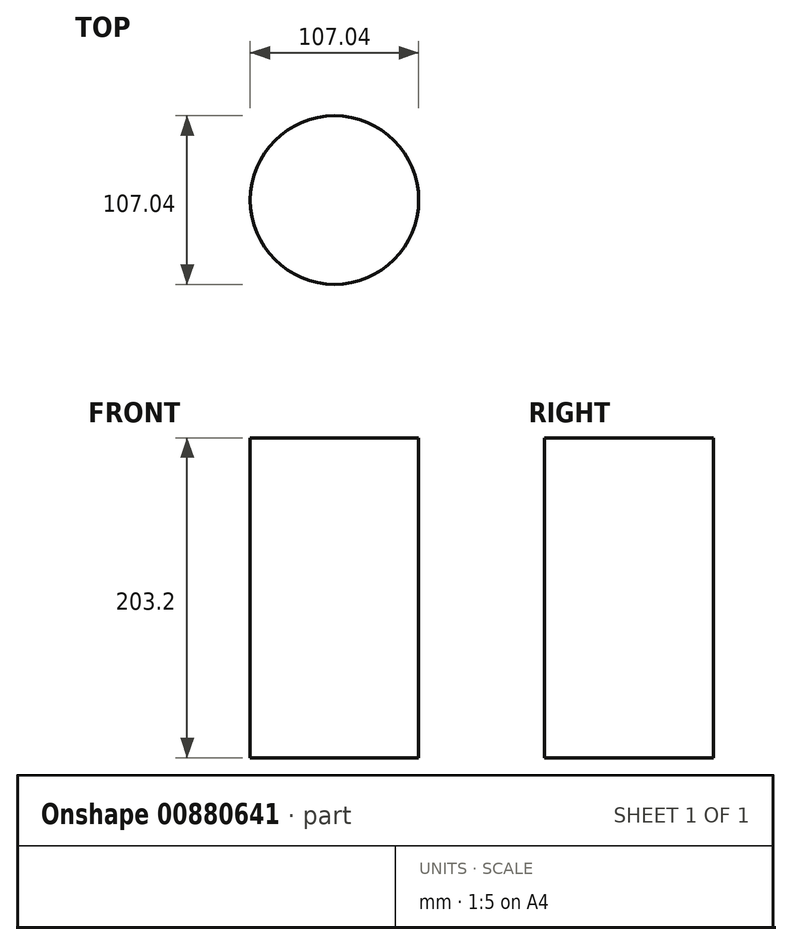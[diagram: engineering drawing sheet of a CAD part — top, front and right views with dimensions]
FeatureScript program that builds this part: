
annotation { "Feature Type Name" : "Feature", "Feature Type Description" : "" }
export const myFeature = defineFeature(function(context is Context, id is Id, definition is map)
    precondition{}
    {
        {
            var Q0;
            Q0=qCreatedBy(makeId("Top.planeOp"),FACE);
            var sketch = newSketch(context, id + "F0", { "sketchPlane" : qUnion([Q0])});
            skCircle(sketch, "E0", {"center": v(0, 0) * mm, "radius": 53.52 * mm});
            skSolve(sketch);
        }
        {
            var Q0;
            Q0=makeQuery(id+"F0.imprint","IMPRINT",FACE,{"disambiguationData":[TD([[makeQuery(id+"F0.imprint","IMPRINT",EDGE,{"derivedFrom":sQuery(id+"F0.wireOp",EDGE,"E0")}),1.0]])]});
            extrude(context, id + "F1", {"entities" : qUnion([Q0]), "depth" : 203.2 * mm, "offsetDistance" : 25.4 * mm});
        }
    });
